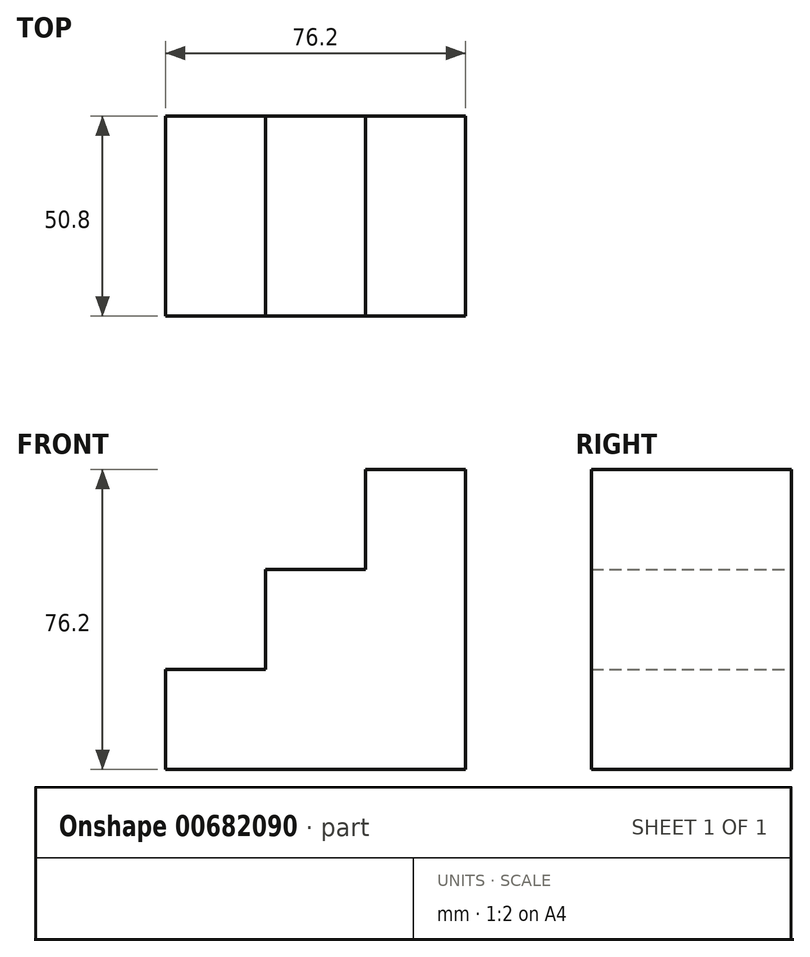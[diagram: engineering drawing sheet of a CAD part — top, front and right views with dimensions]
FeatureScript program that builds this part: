
annotation { "Feature Type Name" : "Feature", "Feature Type Description" : "" }
export const myFeature = defineFeature(function(context is Context, id is Id, definition is map)
    precondition{}
    {
        {
            var Q0;
            Q0=qCreatedBy(makeId("Front.planeOp"),FACE);
            var sketch = newSketch(context, id + "F0", { "sketchPlane" : qUnion([Q0])});
            skLineSegment(sketch, "E0", {"start": v(0, 0) * mm, "end": v(76.2, 0) * mm});
            skLineSegment(sketch, "E1", {"start": v(76.2, 0) * mm, "end": v(76.2, 76.2) * mm});
            skLineSegment(sketch, "E2", {"start": v(76.2, 76.2) * mm, "end": v(50.8, 76.2) * mm});
            skLineSegment(sketch, "E3", {"start": v(50.8, 76.2) * mm, "end": v(50.8, 50.8) * mm});
            skLineSegment(sketch, "E4", {"start": v(50.8, 50.8) * mm, "end": v(25.4, 50.8) * mm});
            skLineSegment(sketch, "E5", {"start": v(25.4, 50.8) * mm, "end": v(25.4, 25.4) * mm});
            skLineSegment(sketch, "E6", {"start": v(25.4, 25.4) * mm, "end": v(0, 25.4) * mm});
            skLineSegment(sketch, "E7", {"start": v(0, 25.4) * mm, "end": v(0, 0) * mm});
            skSolve(sketch);
        }
        {
            var Q0;
            Q0 = qSketchRegion(id + "F0", true);
            extrude(context, id + "F1", {"entities" : qUnion([Q0]), "depth" : 50.8 * mm, "offsetDistance" : 25.4 * mm});
        }
    });
